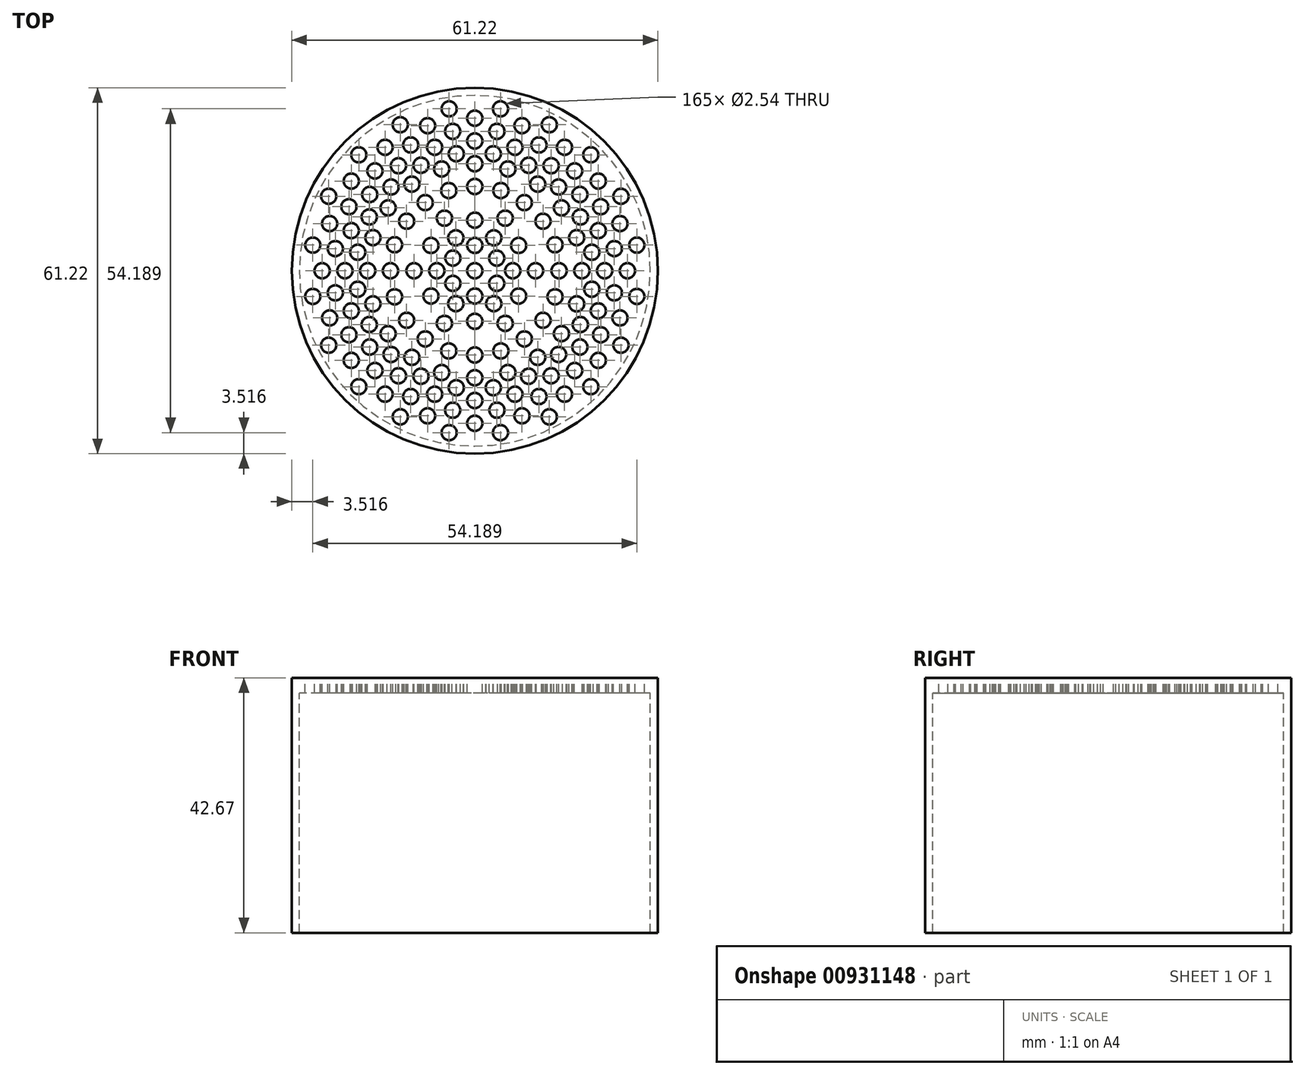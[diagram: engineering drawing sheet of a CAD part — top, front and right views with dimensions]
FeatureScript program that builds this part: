
annotation { "Feature Type Name" : "Feature", "Feature Type Description" : "" }
export const myFeature = defineFeature(function(context is Context, id is Id, definition is map)
    precondition{}
    {
        {
            var Q0;
            Q0=qCreatedBy(makeId("Top.planeOp"),FACE);
            var sketch = newSketch(context, id + "F0", { "sketchPlane" : qUnion([Q0])});
            skCircle(sketch, "E0", {"center": v(0, 0) * mm, "radius": 29.34 * mm});
            skCircle(sketch, "E1", {"center": v(0, 0) * mm, "radius": 30.6 * mm});
            skSolve(sketch);
        }
        {
            var Q0;
            Q0 = qSketchRegion(id + "F0", true);
            extrude(context, id + "F1", {"entities" : qUnion([Q0]), "oppositeDirection" : true, "depth" : 42.67 * mm, "offsetDistance" : 25.4 * mm});
        }
        {
            var Q0;
            Q0=qCreatedBy(makeId("Top.planeOp"),FACE);
            var sketch = newSketch(context, id + "F2", { "sketchPlane" : qUnion([Q0])});
            skCircle(sketch, "E2", {"center": v(0, 0) * mm, "radius": 29.34 * mm});
            skCircle(sketch, "E3", {"center": v(0, 0) * mm, "radius": 1.27 * mm});
            skCircle(sketch, "E4", {"center": v(0, -14.1) * mm, "radius": 1.27 * mm});
            skCircle(sketch, "E5", {"center": v(0, -17.9) * mm, "radius": 1.27 * mm});
            skCircle(sketch, "E6", {"center": v(0, -21.72) * mm, "radius": 1.27 * mm});
            skCircle(sketch, "E7", {"center": v(0, -25.53) * mm, "radius": 1.27 * mm});
            skPoint(sketch, "E8", {"position": v(0, -29.34) * mm});
            skPoint(sketch, "E9.center", {"position": v(0, -2.92) * mm});
            skLineSegment(sketch, "E9.anchor1", {"start": v(0, -2.92) * mm, "end": v(0, -21.72) * mm, "construction": true});
            skCircle(sketch, "E10.1.2", {"center": v(7.89, -24.28) * mm, "radius": 1.27 * mm});
            skCircle(sketch, "E10.1.3", {"center": v(6.71, -20.65) * mm, "radius": 1.27 * mm});
            skCircle(sketch, "E10.1.4", {"center": v(4.36, -13.4) * mm, "radius": 1.27 * mm});
            skCircle(sketch, "E10.1.5", {"center": v(5.53, -17.03) * mm, "radius": 1.27 * mm});
            skPoint(sketch, "E10.1.6", {"position": v(0.9, -2.78) * mm});
            skLineSegment(sketch, "E10.1.7", {"start": v(0.9, -2.78) * mm, "end": v(6.71, -20.65) * mm, "construction": true});
            skCircle(sketch, "E10.2.2", {"center": v(15, -20.65) * mm, "radius": 1.27 * mm});
            skCircle(sketch, "E10.2.3", {"center": v(12.76, -17.57) * mm, "radius": 1.27 * mm});
            skCircle(sketch, "E10.2.4", {"center": v(8.29, -11.4) * mm, "radius": 1.27 * mm});
            skCircle(sketch, "E10.2.5", {"center": v(10.53, -14.49) * mm, "radius": 1.27 * mm});
            skPoint(sketch, "E10.2.6", {"position": v(1.72, -2.36) * mm});
            skLineSegment(sketch, "E10.2.7", {"start": v(1.72, -2.36) * mm, "end": v(12.76, -17.57) * mm, "construction": true});
            skCircle(sketch, "E11.4.3.0", {"center": v(20.65, -15) * mm, "radius": 1.27 * mm});
            skCircle(sketch, "E11.6.3.0", {"center": v(17.57, -12.76) * mm, "radius": 1.27 * mm});
            skCircle(sketch, "E11.8.3.0", {"center": v(11.4, -8.29) * mm, "radius": 1.27 * mm});
            skCircle(sketch, "E11.10.3.0", {"center": v(14.49, -10.53) * mm, "radius": 1.27 * mm});
            skPoint(sketch, "E11.12.3.0", {"position": v(2.36, -1.72) * mm});
            skLineSegment(sketch, "E11.13.3.0", {"start": v(2.36, -1.72) * mm, "end": v(17.57, -12.76) * mm, "construction": true});
            skCircle(sketch, "E11.4.4.0", {"center": v(24.28, -7.89) * mm, "radius": 1.27 * mm});
            skCircle(sketch, "E11.6.4.0", {"center": v(20.65, -6.71) * mm, "radius": 1.27 * mm});
            skCircle(sketch, "E11.8.4.0", {"center": v(13.4, -4.36) * mm, "radius": 1.27 * mm});
            skCircle(sketch, "E11.10.4.0", {"center": v(17.03, -5.53) * mm, "radius": 1.27 * mm});
            skPoint(sketch, "E11.12.4.0", {"position": v(2.78, -0.9) * mm});
            skLineSegment(sketch, "E11.13.4.0", {"start": v(2.78, -0.9) * mm, "end": v(20.65, -6.71) * mm, "construction": true});
            skCircle(sketch, "E11.4.5.0", {"center": v(25.53, 0) * mm, "radius": 1.27 * mm});
            skCircle(sketch, "E11.6.5.0", {"center": v(21.72, 0) * mm, "radius": 1.27 * mm});
            skCircle(sketch, "E11.8.5.0", {"center": v(14.1, 0) * mm, "radius": 1.27 * mm});
            skCircle(sketch, "E11.10.5.0", {"center": v(17.9, 0) * mm, "radius": 1.27 * mm});
            skPoint(sketch, "E11.12.5.0", {"position": v(2.92, 0) * mm});
            skLineSegment(sketch, "E11.13.5.0", {"start": v(2.92, 0) * mm, "end": v(21.72, 0) * mm, "construction": true});
            skCircle(sketch, "E11.4.6.0", {"center": v(24.28, 7.89) * mm, "radius": 1.27 * mm});
            skCircle(sketch, "E11.6.6.0", {"center": v(20.65, 6.71) * mm, "radius": 1.27 * mm});
            skCircle(sketch, "E11.8.6.0", {"center": v(13.4, 4.36) * mm, "radius": 1.27 * mm});
            skCircle(sketch, "E11.10.6.0", {"center": v(17.03, 5.53) * mm, "radius": 1.27 * mm});
            skPoint(sketch, "E11.12.6.0", {"position": v(2.78, 0.9) * mm});
            skLineSegment(sketch, "E11.13.6.0", {"start": v(2.78, 0.9) * mm, "end": v(20.65, 6.71) * mm, "construction": true});
            skCircle(sketch, "E11.4.7.0", {"center": v(20.65, 15) * mm, "radius": 1.27 * mm});
            skCircle(sketch, "E11.6.7.0", {"center": v(17.57, 12.76) * mm, "radius": 1.27 * mm});
            skCircle(sketch, "E11.8.7.0", {"center": v(11.4, 8.29) * mm, "radius": 1.27 * mm});
            skCircle(sketch, "E11.10.7.0", {"center": v(14.49, 10.53) * mm, "radius": 1.27 * mm});
            skPoint(sketch, "E11.12.7.0", {"position": v(2.36, 1.72) * mm});
            skLineSegment(sketch, "E11.13.7.0", {"start": v(2.36, 1.72) * mm, "end": v(17.57, 12.76) * mm, "construction": true});
            skCircle(sketch, "E12.4.8.0", {"center": v(15, 20.65) * mm, "radius": 1.27 * mm});
            skCircle(sketch, "E12.6.8.0", {"center": v(12.76, 17.57) * mm, "radius": 1.27 * mm});
            skCircle(sketch, "E12.8.8.0", {"center": v(8.29, 11.4) * mm, "radius": 1.27 * mm});
            skCircle(sketch, "E12.10.8.0", {"center": v(10.53, 14.49) * mm, "radius": 1.27 * mm});
            skPoint(sketch, "E12.12.8.0", {"position": v(1.72, 2.36) * mm});
            skLineSegment(sketch, "E12.13.8.0", {"start": v(1.72, 2.36) * mm, "end": v(12.76, 17.57) * mm, "construction": true});
            skCircle(sketch, "E12.4.9.0", {"center": v(7.89, 24.28) * mm, "radius": 1.27 * mm});
            skCircle(sketch, "E12.6.9.0", {"center": v(6.71, 20.65) * mm, "radius": 1.27 * mm});
            skCircle(sketch, "E12.8.9.0", {"center": v(4.36, 13.4) * mm, "radius": 1.27 * mm});
            skCircle(sketch, "E12.10.9.0", {"center": v(5.53, 17.03) * mm, "radius": 1.27 * mm});
            skPoint(sketch, "E12.12.9.0", {"position": v(0.9, 2.78) * mm});
            skLineSegment(sketch, "E12.13.9.0", {"start": v(0.9, 2.78) * mm, "end": v(6.71, 20.65) * mm, "construction": true});
            skCircle(sketch, "E12.4.10.0", {"center": v(0, 25.53) * mm, "radius": 1.27 * mm});
            skCircle(sketch, "E12.6.10.0", {"center": v(0, 21.72) * mm, "radius": 1.27 * mm});
            skCircle(sketch, "E12.8.10.0", {"center": v(0, 14.1) * mm, "radius": 1.27 * mm});
            skCircle(sketch, "E12.10.10.0", {"center": v(0, 17.9) * mm, "radius": 1.27 * mm});
            skPoint(sketch, "E12.12.10.0", {"position": v(0, 2.92) * mm});
            skLineSegment(sketch, "E12.13.10.0", {"start": v(0, 2.92) * mm, "end": v(0, 21.72) * mm, "construction": true});
            skCircle(sketch, "E12.4.11.0", {"center": v(-7.89, 24.28) * mm, "radius": 1.27 * mm});
            skCircle(sketch, "E12.6.11.0", {"center": v(-6.71, 20.65) * mm, "radius": 1.27 * mm});
            skCircle(sketch, "E12.8.11.0", {"center": v(-4.36, 13.4) * mm, "radius": 1.27 * mm});
            skCircle(sketch, "E12.10.11.0", {"center": v(-5.53, 17.03) * mm, "radius": 1.27 * mm});
            skPoint(sketch, "E12.12.11.0", {"position": v(-0.9, 2.78) * mm});
            skLineSegment(sketch, "E12.13.11.0", {"start": v(-0.9, 2.78) * mm, "end": v(-6.71, 20.65) * mm, "construction": true});
            skCircle(sketch, "E12.4.12.0", {"center": v(-15, 20.65) * mm, "radius": 1.27 * mm});
            skCircle(sketch, "E12.6.12.0", {"center": v(-12.76, 17.57) * mm, "radius": 1.27 * mm});
            skCircle(sketch, "E12.8.12.0", {"center": v(-8.29, 11.4) * mm, "radius": 1.27 * mm});
            skCircle(sketch, "E12.10.12.0", {"center": v(-10.53, 14.49) * mm, "radius": 1.27 * mm});
            skPoint(sketch, "E12.12.12.0", {"position": v(-1.72, 2.36) * mm});
            skLineSegment(sketch, "E12.13.12.0", {"start": v(-1.72, 2.36) * mm, "end": v(-12.76, 17.57) * mm, "construction": true});
            skCircle(sketch, "E12.4.13.0", {"center": v(-20.65, 15) * mm, "radius": 1.27 * mm});
            skCircle(sketch, "E12.6.13.0", {"center": v(-17.57, 12.76) * mm, "radius": 1.27 * mm});
            skCircle(sketch, "E12.8.13.0", {"center": v(-11.4, 8.29) * mm, "radius": 1.27 * mm});
            skCircle(sketch, "E12.10.13.0", {"center": v(-14.49, 10.53) * mm, "radius": 1.27 * mm});
            skPoint(sketch, "E12.12.13.0", {"position": v(-2.36, 1.72) * mm});
            skLineSegment(sketch, "E12.13.13.0", {"start": v(-2.36, 1.72) * mm, "end": v(-17.57, 12.76) * mm, "construction": true});
            skCircle(sketch, "E12.4.14.0", {"center": v(-24.28, 7.89) * mm, "radius": 1.27 * mm});
            skCircle(sketch, "E12.6.14.0", {"center": v(-20.65, 6.71) * mm, "radius": 1.27 * mm});
            skCircle(sketch, "E12.8.14.0", {"center": v(-13.4, 4.36) * mm, "radius": 1.27 * mm});
            skCircle(sketch, "E12.10.14.0", {"center": v(-17.03, 5.53) * mm, "radius": 1.27 * mm});
            skPoint(sketch, "E12.12.14.0", {"position": v(-2.78, 0.9) * mm});
            skLineSegment(sketch, "E12.13.14.0", {"start": v(-2.78, 0.9) * mm, "end": v(-20.65, 6.71) * mm, "construction": true});
            skCircle(sketch, "E12.4.15.0", {"center": v(-25.53, 0) * mm, "radius": 1.27 * mm});
            skCircle(sketch, "E12.6.15.0", {"center": v(-21.72, 0) * mm, "radius": 1.27 * mm});
            skCircle(sketch, "E12.8.15.0", {"center": v(-14.1, 0) * mm, "radius": 1.27 * mm});
            skCircle(sketch, "E12.10.15.0", {"center": v(-17.9, 0) * mm, "radius": 1.27 * mm});
            skPoint(sketch, "E12.12.15.0", {"position": v(-2.92, 0) * mm});
            skLineSegment(sketch, "E12.13.15.0", {"start": v(-2.92, 0) * mm, "end": v(-21.72, 0) * mm, "construction": true});
            skCircle(sketch, "E13.4.16.0", {"center": v(-24.28, -7.89) * mm, "radius": 1.27 * mm});
            skCircle(sketch, "E13.6.16.0", {"center": v(-20.65, -6.71) * mm, "radius": 1.27 * mm});
            skCircle(sketch, "E13.8.16.0", {"center": v(-13.4, -4.36) * mm, "radius": 1.27 * mm});
            skCircle(sketch, "E13.10.16.0", {"center": v(-17.03, -5.53) * mm, "radius": 1.27 * mm});
            skPoint(sketch, "E13.12.16.0", {"position": v(-2.78, -0.9) * mm});
            skLineSegment(sketch, "E13.13.16.0", {"start": v(-2.78, -0.9) * mm, "end": v(-20.65, -6.71) * mm, "construction": true});
            skCircle(sketch, "E13.4.17.0", {"center": v(-20.65, -15) * mm, "radius": 1.27 * mm});
            skCircle(sketch, "E13.6.17.0", {"center": v(-17.57, -12.76) * mm, "radius": 1.27 * mm});
            skCircle(sketch, "E13.8.17.0", {"center": v(-11.4, -8.29) * mm, "radius": 1.27 * mm});
            skCircle(sketch, "E13.10.17.0", {"center": v(-14.49, -10.53) * mm, "radius": 1.27 * mm});
            skPoint(sketch, "E13.12.17.0", {"position": v(-2.36, -1.72) * mm});
            skLineSegment(sketch, "E13.13.17.0", {"start": v(-2.36, -1.72) * mm, "end": v(-17.57, -12.76) * mm, "construction": true});
            skCircle(sketch, "E13.4.18.0", {"center": v(-15, -20.65) * mm, "radius": 1.27 * mm});
            skCircle(sketch, "E13.6.18.0", {"center": v(-12.76, -17.57) * mm, "radius": 1.27 * mm});
            skCircle(sketch, "E13.8.18.0", {"center": v(-8.29, -11.4) * mm, "radius": 1.27 * mm});
            skCircle(sketch, "E13.10.18.0", {"center": v(-10.53, -14.49) * mm, "radius": 1.27 * mm});
            skPoint(sketch, "E13.12.18.0", {"position": v(-1.72, -2.36) * mm});
            skLineSegment(sketch, "E13.13.18.0", {"start": v(-1.72, -2.36) * mm, "end": v(-12.76, -17.57) * mm, "construction": true});
            skCircle(sketch, "E13.4.19.0", {"center": v(-7.89, -24.28) * mm, "radius": 1.27 * mm});
            skCircle(sketch, "E13.6.19.0", {"center": v(-6.71, -20.65) * mm, "radius": 1.27 * mm});
            skCircle(sketch, "E13.8.19.0", {"center": v(-4.36, -13.4) * mm, "radius": 1.27 * mm});
            skCircle(sketch, "E13.10.19.0", {"center": v(-5.53, -17.03) * mm, "radius": 1.27 * mm});
            skPoint(sketch, "E13.12.19.0", {"position": v(-0.9, -2.78) * mm});
            skLineSegment(sketch, "E13.13.19.0", {"start": v(-0.9, -2.78) * mm, "end": v(-6.71, -20.65) * mm, "construction": true});
            skSolve(sketch);
        }
        {
            var Q0;
            Q0 = qSketchRegion(id + "F2", true);
            extrude(context, id + "F3", {"entities" : qUnion([Q0]), "operationType" : NewBodyOperationType.ADD, "oppositeDirection" : true, "depth" : 2.54 * mm, "offsetDistance" : 25.4 * mm});
        }
        {
            var Q0;
            Q0=makeQuery(id+"F3.opExtrude","CAP_FACE",FACE,{"disambiguationData":[OSD([sQuery(id+"F2.wireOp",EDGE,"E2"),sQuery(id+"F2.wireOp",EDGE,"E4"),sQuery(id+"F2.wireOp",EDGE,"E5"),sQuery(id+"F2.wireOp",EDGE,"E6"),sQuery(id+"F2.wireOp",EDGE,"E7"),sQuery(id+"F2.wireOp",EDGE,"E10.1.2"),sQuery(id+"F2.wireOp",EDGE,"E10.1.3"),sQuery(id+"F2.wireOp",EDGE,"E10.1.4"),sQuery(id+"F2.wireOp",EDGE,"E10.1.5"),sQuery(id+"F2.wireOp",EDGE,"E10.2.2"),sQuery(id+"F2.wireOp",EDGE,"E10.2.3"),sQuery(id+"F2.wireOp",EDGE,"E10.2.4"),sQuery(id+"F2.wireOp",EDGE,"E10.2.5"),sQuery(id+"F2.wireOp",EDGE,"E11.4.3.0"),sQuery(id+"F2.wireOp",EDGE,"E11.6.3.0"),sQuery(id+"F2.wireOp",EDGE,"E11.8.3.0"),sQuery(id+"F2.wireOp",EDGE,"E11.10.3.0"),sQuery(id+"F2.wireOp",EDGE,"E11.4.4.0"),sQuery(id+"F2.wireOp",EDGE,"E11.6.4.0"),sQuery(id+"F2.wireOp",EDGE,"E11.8.4.0"),sQuery(id+"F2.wireOp",EDGE,"E11.10.4.0"),sQuery(id+"F2.wireOp",EDGE,"E11.4.5.0"),sQuery(id+"F2.wireOp",EDGE,"E11.6.5.0"),sQuery(id+"F2.wireOp",EDGE,"E11.8.5.0"),sQuery(id+"F2.wireOp",EDGE,"E11.10.5.0"),sQuery(id+"F2.wireOp",EDGE,"E11.4.6.0"),sQuery(id+"F2.wireOp",EDGE,"E11.6.6.0"),sQuery(id+"F2.wireOp",EDGE,"E11.8.6.0"),sQuery(id+"F2.wireOp",EDGE,"E11.10.6.0"),sQuery(id+"F2.wireOp",EDGE,"E11.4.7.0"),sQuery(id+"F2.wireOp",EDGE,"E11.6.7.0"),sQuery(id+"F2.wireOp",EDGE,"E11.8.7.0"),sQuery(id+"F2.wireOp",EDGE,"E11.10.7.0"),sQuery(id+"F2.wireOp",EDGE,"E12.4.8.0"),sQuery(id+"F2.wireOp",EDGE,"E12.6.8.0"),sQuery(id+"F2.wireOp",EDGE,"E12.8.8.0"),sQuery(id+"F2.wireOp",EDGE,"E12.10.8.0"),sQuery(id+"F2.wireOp",EDGE,"E12.4.9.0"),sQuery(id+"F2.wireOp",EDGE,"E12.6.9.0"),sQuery(id+"F2.wireOp",EDGE,"E12.8.9.0"),sQuery(id+"F2.wireOp",EDGE,"E12.10.9.0"),sQuery(id+"F2.wireOp",EDGE,"E12.4.10.0"),sQuery(id+"F2.wireOp",EDGE,"E12.6.10.0"),sQuery(id+"F2.wireOp",EDGE,"E12.8.10.0"),sQuery(id+"F2.wireOp",EDGE,"E12.10.10.0"),sQuery(id+"F2.wireOp",EDGE,"E12.4.11.0"),sQuery(id+"F2.wireOp",EDGE,"E12.6.11.0"),sQuery(id+"F2.wireOp",EDGE,"E12.8.11.0"),sQuery(id+"F2.wireOp",EDGE,"E12.10.11.0"),sQuery(id+"F2.wireOp",EDGE,"E12.4.12.0"),sQuery(id+"F2.wireOp",EDGE,"E12.6.12.0"),sQuery(id+"F2.wireOp",EDGE,"E12.8.12.0"),sQuery(id+"F2.wireOp",EDGE,"E12.10.12.0"),sQuery(id+"F2.wireOp",EDGE,"E12.4.13.0"),sQuery(id+"F2.wireOp",EDGE,"E12.6.13.0"),sQuery(id+"F2.wireOp",EDGE,"E12.8.13.0"),sQuery(id+"F2.wireOp",EDGE,"E12.10.13.0"),sQuery(id+"F2.wireOp",EDGE,"E12.4.14.0"),sQuery(id+"F2.wireOp",EDGE,"E12.6.14.0"),sQuery(id+"F2.wireOp",EDGE,"E12.8.14.0"),sQuery(id+"F2.wireOp",EDGE,"E12.10.14.0"),sQuery(id+"F2.wireOp",EDGE,"E12.4.15.0"),sQuery(id+"F2.wireOp",EDGE,"E12.6.15.0"),sQuery(id+"F2.wireOp",EDGE,"E12.8.15.0"),sQuery(id+"F2.wireOp",EDGE,"E12.10.15.0"),sQuery(id+"F2.wireOp",EDGE,"E13.4.16.0"),sQuery(id+"F2.wireOp",EDGE,"E13.6.16.0"),sQuery(id+"F2.wireOp",EDGE,"E13.8.16.0"),sQuery(id+"F2.wireOp",EDGE,"E13.10.16.0"),sQuery(id+"F2.wireOp",EDGE,"E13.4.17.0"),sQuery(id+"F2.wireOp",EDGE,"E13.6.17.0"),sQuery(id+"F2.wireOp",EDGE,"E13.8.17.0"),sQuery(id+"F2.wireOp",EDGE,"E13.10.17.0"),sQuery(id+"F2.wireOp",EDGE,"E13.4.18.0"),sQuery(id+"F2.wireOp",EDGE,"E13.6.18.0"),sQuery(id+"F2.wireOp",EDGE,"E13.8.18.0"),sQuery(id+"F2.wireOp",EDGE,"E13.10.18.0"),sQuery(id+"F2.wireOp",EDGE,"E13.4.19.0"),sQuery(id+"F2.wireOp",EDGE,"E3"),sQuery(id+"F2.wireOp",EDGE,"E13.6.19.0"),sQuery(id+"F2.wireOp",EDGE,"E13.8.19.0"),sQuery(id+"F2.wireOp",EDGE,"E13.10.19.0")])],"isStart":true});
            var sketch = newSketch(context, id + "F4", { "sketchPlane" : qUnion([Q0])});
            skCircle(sketch, "E14", {"center": v(-3.7, -23.33) * mm, "radius": 1.27 * mm});
            skCircle(sketch, "E15", {"center": v(-4.3, -27.1) * mm, "radius": 1.27 * mm});
            skLineSegment(sketch, "E16", {"start": v(0, 0) * mm, "end": v(-5.46, -34.46) * mm});
            skPoint(sketch, "E17", {"position": v(-4.59, -28.98) * mm});
            skCircle(sketch, "E18.1.0", {"center": v(4.3, -27.1) * mm, "radius": 1.27 * mm});
            skCircle(sketch, "E18.1.1", {"center": v(3.7, -23.33) * mm, "radius": 1.27 * mm});
            skCircle(sketch, "E18.2.0", {"center": v(12.45, -24.44) * mm, "radius": 1.27 * mm});
            skCircle(sketch, "E18.2.1", {"center": v(10.72, -21.05) * mm, "radius": 1.27 * mm});
            skCircle(sketch, "E18.3.0", {"center": v(19.4, -19.4) * mm, "radius": 1.27 * mm});
            skCircle(sketch, "E18.3.1", {"center": v(16.7, -16.7) * mm, "radius": 1.27 * mm});
            skCircle(sketch, "E18.4.0", {"center": v(24.44, -12.45) * mm, "radius": 1.27 * mm});
            skCircle(sketch, "E18.4.1", {"center": v(21.05, -10.72) * mm, "radius": 1.27 * mm});
            skCircle(sketch, "E18.5.0", {"center": v(27.1, -4.3) * mm, "radius": 1.27 * mm});
            skCircle(sketch, "E18.5.1", {"center": v(23.33, -3.7) * mm, "radius": 1.27 * mm});
            skCircle(sketch, "E18.6.0", {"center": v(27.1, 4.3) * mm, "radius": 1.27 * mm});
            skCircle(sketch, "E18.6.1", {"center": v(23.33, 3.7) * mm, "radius": 1.27 * mm});
            skCircle(sketch, "E18.7.0", {"center": v(24.44, 12.45) * mm, "radius": 1.27 * mm});
            skCircle(sketch, "E18.7.1", {"center": v(21.05, 10.72) * mm, "radius": 1.27 * mm});
            skCircle(sketch, "E18.8.0", {"center": v(19.4, 19.4) * mm, "radius": 1.27 * mm});
            skCircle(sketch, "E18.8.1", {"center": v(16.7, 16.7) * mm, "radius": 1.27 * mm});
            skCircle(sketch, "E18.9.0", {"center": v(12.45, 24.44) * mm, "radius": 1.27 * mm});
            skCircle(sketch, "E18.9.1", {"center": v(10.72, 21.05) * mm, "radius": 1.27 * mm});
            skCircle(sketch, "E18.10.0", {"center": v(4.3, 27.1) * mm, "radius": 1.27 * mm});
            skCircle(sketch, "E18.10.1", {"center": v(3.7, 23.33) * mm, "radius": 1.27 * mm});
            skCircle(sketch, "E18.11.0", {"center": v(-4.3, 27.1) * mm, "radius": 1.27 * mm});
            skCircle(sketch, "E18.11.1", {"center": v(-3.7, 23.33) * mm, "radius": 1.27 * mm});
            skCircle(sketch, "E18.12.0", {"center": v(-12.45, 24.44) * mm, "radius": 1.27 * mm});
            skCircle(sketch, "E18.12.1", {"center": v(-10.72, 21.05) * mm, "radius": 1.27 * mm});
            skCircle(sketch, "E18.13.0", {"center": v(-19.4, 19.4) * mm, "radius": 1.27 * mm});
            skCircle(sketch, "E18.13.1", {"center": v(-16.7, 16.7) * mm, "radius": 1.27 * mm});
            skCircle(sketch, "E18.14.0", {"center": v(-24.44, 12.45) * mm, "radius": 1.27 * mm});
            skCircle(sketch, "E18.14.1", {"center": v(-21.05, 10.72) * mm, "radius": 1.27 * mm});
            skCircle(sketch, "E18.15.0", {"center": v(-27.1, 4.3) * mm, "radius": 1.27 * mm});
            skCircle(sketch, "E18.15.1", {"center": v(-23.33, 3.7) * mm, "radius": 1.27 * mm});
            skCircle(sketch, "E18.16.0", {"center": v(-27.1, -4.3) * mm, "radius": 1.27 * mm});
            skCircle(sketch, "E18.16.1", {"center": v(-23.33, -3.7) * mm, "radius": 1.27 * mm});
            skCircle(sketch, "E18.17.0", {"center": v(-24.44, -12.45) * mm, "radius": 1.27 * mm});
            skCircle(sketch, "E18.17.1", {"center": v(-21.05, -10.72) * mm, "radius": 1.27 * mm});
            skCircle(sketch, "E18.18.0", {"center": v(-19.4, -19.4) * mm, "radius": 1.27 * mm});
            skCircle(sketch, "E18.18.1", {"center": v(-16.7, -16.7) * mm, "radius": 1.27 * mm});
            skCircle(sketch, "E18.19.0", {"center": v(-12.45, -24.44) * mm, "radius": 1.27 * mm});
            skCircle(sketch, "E18.19.1", {"center": v(-10.72, -21.05) * mm, "radius": 1.27 * mm});
            skPoint(sketch, "E18.center", {"position": v(0, 0) * mm});
            skCircle(sketch, "E19", {"center": v(-3.1, -19.57) * mm, "radius": 1.27 * mm});
            skCircle(sketch, "E20.1.0", {"center": v(3.1, -19.57) * mm, "radius": 1.27 * mm});
            skCircle(sketch, "E20.2.0", {"center": v(9, -17.65) * mm, "radius": 1.27 * mm});
            skCircle(sketch, "E20.3.0", {"center": v(14, -14) * mm, "radius": 1.27 * mm});
            skCircle(sketch, "E20.4.0", {"center": v(17.65, -9) * mm, "radius": 1.27 * mm});
            skCircle(sketch, "E20.5.0", {"center": v(19.57, -3.1) * mm, "radius": 1.27 * mm});
            skCircle(sketch, "E20.6.0", {"center": v(19.57, 3.1) * mm, "radius": 1.27 * mm});
            skCircle(sketch, "E20.7.0", {"center": v(17.65, 9) * mm, "radius": 1.27 * mm});
            skCircle(sketch, "E20.8.0", {"center": v(14, 14) * mm, "radius": 1.27 * mm});
            skCircle(sketch, "E20.9.0", {"center": v(9, 17.65) * mm, "radius": 1.27 * mm});
            skCircle(sketch, "E20.10.0", {"center": v(3.1, 19.57) * mm, "radius": 1.27 * mm});
            skCircle(sketch, "E20.11.0", {"center": v(-3.1, 19.57) * mm, "radius": 1.27 * mm});
            skCircle(sketch, "E20.12.0", {"center": v(-9, 17.65) * mm, "radius": 1.27 * mm});
            skCircle(sketch, "E20.13.0", {"center": v(-14, 14) * mm, "radius": 1.27 * mm});
            skCircle(sketch, "E20.14.0", {"center": v(-17.65, 9) * mm, "radius": 1.27 * mm});
            skCircle(sketch, "E20.15.0", {"center": v(-19.57, 3.1) * mm, "radius": 1.27 * mm});
            skCircle(sketch, "E20.16.0", {"center": v(-19.57, -3.1) * mm, "radius": 1.27 * mm});
            skCircle(sketch, "E20.17.0", {"center": v(-17.65, -9) * mm, "radius": 1.27 * mm});
            skCircle(sketch, "E20.18.0", {"center": v(-14, -14) * mm, "radius": 1.27 * mm});
            skCircle(sketch, "E20.19.0", {"center": v(-9, -17.65) * mm, "radius": 1.27 * mm});
            skSolve(sketch);
        }
        {
            var Q0;
            Q0=makeQuery(id+"F3.opExtrude","CAP_FACE",FACE,{"disambiguationData":[OSD([sQuery(id+"F2.wireOp",EDGE,"E2"),sQuery(id+"F2.wireOp",EDGE,"E4"),sQuery(id+"F2.wireOp",EDGE,"E5"),sQuery(id+"F2.wireOp",EDGE,"E6"),sQuery(id+"F2.wireOp",EDGE,"E7"),sQuery(id+"F2.wireOp",EDGE,"E10.1.2"),sQuery(id+"F2.wireOp",EDGE,"E10.1.3"),sQuery(id+"F2.wireOp",EDGE,"E10.1.4"),sQuery(id+"F2.wireOp",EDGE,"E10.1.5"),sQuery(id+"F2.wireOp",EDGE,"E10.2.2"),sQuery(id+"F2.wireOp",EDGE,"E10.2.3"),sQuery(id+"F2.wireOp",EDGE,"E10.2.4"),sQuery(id+"F2.wireOp",EDGE,"E10.2.5"),sQuery(id+"F2.wireOp",EDGE,"E11.4.3.0"),sQuery(id+"F2.wireOp",EDGE,"E11.6.3.0"),sQuery(id+"F2.wireOp",EDGE,"E11.8.3.0"),sQuery(id+"F2.wireOp",EDGE,"E11.10.3.0"),sQuery(id+"F2.wireOp",EDGE,"E11.4.4.0"),sQuery(id+"F2.wireOp",EDGE,"E11.6.4.0"),sQuery(id+"F2.wireOp",EDGE,"E11.8.4.0"),sQuery(id+"F2.wireOp",EDGE,"E11.10.4.0"),sQuery(id+"F2.wireOp",EDGE,"E11.4.5.0"),sQuery(id+"F2.wireOp",EDGE,"E11.6.5.0"),sQuery(id+"F2.wireOp",EDGE,"E11.8.5.0"),sQuery(id+"F2.wireOp",EDGE,"E11.10.5.0"),sQuery(id+"F2.wireOp",EDGE,"E11.4.6.0"),sQuery(id+"F2.wireOp",EDGE,"E11.6.6.0"),sQuery(id+"F2.wireOp",EDGE,"E11.8.6.0"),sQuery(id+"F2.wireOp",EDGE,"E11.10.6.0"),sQuery(id+"F2.wireOp",EDGE,"E11.4.7.0"),sQuery(id+"F2.wireOp",EDGE,"E11.6.7.0"),sQuery(id+"F2.wireOp",EDGE,"E11.8.7.0"),sQuery(id+"F2.wireOp",EDGE,"E11.10.7.0"),sQuery(id+"F2.wireOp",EDGE,"E12.4.8.0"),sQuery(id+"F2.wireOp",EDGE,"E12.6.8.0"),sQuery(id+"F2.wireOp",EDGE,"E12.8.8.0"),sQuery(id+"F2.wireOp",EDGE,"E12.10.8.0"),sQuery(id+"F2.wireOp",EDGE,"E12.4.9.0"),sQuery(id+"F2.wireOp",EDGE,"E12.6.9.0"),sQuery(id+"F2.wireOp",EDGE,"E12.8.9.0"),sQuery(id+"F2.wireOp",EDGE,"E12.10.9.0"),sQuery(id+"F2.wireOp",EDGE,"E12.4.10.0"),sQuery(id+"F2.wireOp",EDGE,"E12.6.10.0"),sQuery(id+"F2.wireOp",EDGE,"E12.8.10.0"),sQuery(id+"F2.wireOp",EDGE,"E12.10.10.0"),sQuery(id+"F2.wireOp",EDGE,"E12.4.11.0"),sQuery(id+"F2.wireOp",EDGE,"E12.6.11.0"),sQuery(id+"F2.wireOp",EDGE,"E12.8.11.0"),sQuery(id+"F2.wireOp",EDGE,"E12.10.11.0"),sQuery(id+"F2.wireOp",EDGE,"E12.4.12.0"),sQuery(id+"F2.wireOp",EDGE,"E12.6.12.0"),sQuery(id+"F2.wireOp",EDGE,"E12.8.12.0"),sQuery(id+"F2.wireOp",EDGE,"E12.10.12.0"),sQuery(id+"F2.wireOp",EDGE,"E12.4.13.0"),sQuery(id+"F2.wireOp",EDGE,"E12.6.13.0"),sQuery(id+"F2.wireOp",EDGE,"E12.8.13.0"),sQuery(id+"F2.wireOp",EDGE,"E12.10.13.0"),sQuery(id+"F2.wireOp",EDGE,"E12.4.14.0"),sQuery(id+"F2.wireOp",EDGE,"E12.6.14.0"),sQuery(id+"F2.wireOp",EDGE,"E12.8.14.0"),sQuery(id+"F2.wireOp",EDGE,"E12.10.14.0"),sQuery(id+"F2.wireOp",EDGE,"E12.4.15.0"),sQuery(id+"F2.wireOp",EDGE,"E12.6.15.0"),sQuery(id+"F2.wireOp",EDGE,"E12.8.15.0"),sQuery(id+"F2.wireOp",EDGE,"E12.10.15.0"),sQuery(id+"F2.wireOp",EDGE,"E13.4.16.0"),sQuery(id+"F2.wireOp",EDGE,"E13.6.16.0"),sQuery(id+"F2.wireOp",EDGE,"E13.8.16.0"),sQuery(id+"F2.wireOp",EDGE,"E13.10.16.0"),sQuery(id+"F2.wireOp",EDGE,"E13.4.17.0"),sQuery(id+"F2.wireOp",EDGE,"E13.6.17.0"),sQuery(id+"F2.wireOp",EDGE,"E13.8.17.0"),sQuery(id+"F2.wireOp",EDGE,"E13.10.17.0"),sQuery(id+"F2.wireOp",EDGE,"E13.4.18.0"),sQuery(id+"F2.wireOp",EDGE,"E13.6.18.0"),sQuery(id+"F2.wireOp",EDGE,"E13.8.18.0"),sQuery(id+"F2.wireOp",EDGE,"E13.10.18.0"),sQuery(id+"F2.wireOp",EDGE,"E13.4.19.0"),sQuery(id+"F2.wireOp",EDGE,"E3"),sQuery(id+"F2.wireOp",EDGE,"E13.6.19.0"),sQuery(id+"F2.wireOp",EDGE,"E13.8.19.0"),sQuery(id+"F2.wireOp",EDGE,"E13.10.19.0")])],"isStart":true});
            var sketch = newSketch(context, id + "F5", { "sketchPlane" : qUnion([Q0])});
            skCircle(sketch, "E21", {"center": v(0, -4.23) * mm, "radius": 1.27 * mm});
            skCircle(sketch, "E22", {"center": v(0, -8.47) * mm, "radius": 1.27 * mm});
            skCircle(sketch, "E23.1.0", {"center": v(3.67, -2.12) * mm, "radius": 1.27 * mm});
            skCircle(sketch, "E23.1.1", {"center": v(7.33, -4.23) * mm, "radius": 1.27 * mm});
            skCircle(sketch, "E23.2.0", {"center": v(3.67, 2.12) * mm, "radius": 1.27 * mm});
            skCircle(sketch, "E23.2.1", {"center": v(7.33, 4.23) * mm, "radius": 1.27 * mm});
            skCircle(sketch, "E23.3.0", {"center": v(0, 4.23) * mm, "radius": 1.27 * mm});
            skCircle(sketch, "E23.3.1", {"center": v(0, 8.47) * mm, "radius": 1.27 * mm});
            skCircle(sketch, "E23.4.0", {"center": v(-3.67, 2.12) * mm, "radius": 1.27 * mm});
            skCircle(sketch, "E23.4.1", {"center": v(-7.33, 4.23) * mm, "radius": 1.27 * mm});
            skCircle(sketch, "E23.5.0", {"center": v(-3.67, -2.12) * mm, "radius": 1.27 * mm});
            skCircle(sketch, "E23.5.1", {"center": v(-7.33, -4.23) * mm, "radius": 1.27 * mm});
            skPoint(sketch, "E23.center", {"position": v(0, 0) * mm});
            skSolve(sketch);
        }
        {
            var Q0;
            Q0=makeQuery(id+"F3.opExtrude","CAP_FACE",FACE,{"disambiguationData":[OSD([sQuery(id+"F2.wireOp",EDGE,"E2"),sQuery(id+"F2.wireOp",EDGE,"E4"),sQuery(id+"F2.wireOp",EDGE,"E5"),sQuery(id+"F2.wireOp",EDGE,"E6"),sQuery(id+"F2.wireOp",EDGE,"E7"),sQuery(id+"F2.wireOp",EDGE,"E10.1.2"),sQuery(id+"F2.wireOp",EDGE,"E10.1.3"),sQuery(id+"F2.wireOp",EDGE,"E10.1.4"),sQuery(id+"F2.wireOp",EDGE,"E10.1.5"),sQuery(id+"F2.wireOp",EDGE,"E10.2.2"),sQuery(id+"F2.wireOp",EDGE,"E10.2.3"),sQuery(id+"F2.wireOp",EDGE,"E10.2.4"),sQuery(id+"F2.wireOp",EDGE,"E10.2.5"),sQuery(id+"F2.wireOp",EDGE,"E11.4.3.0"),sQuery(id+"F2.wireOp",EDGE,"E11.6.3.0"),sQuery(id+"F2.wireOp",EDGE,"E11.8.3.0"),sQuery(id+"F2.wireOp",EDGE,"E11.10.3.0"),sQuery(id+"F2.wireOp",EDGE,"E11.4.4.0"),sQuery(id+"F2.wireOp",EDGE,"E11.6.4.0"),sQuery(id+"F2.wireOp",EDGE,"E11.8.4.0"),sQuery(id+"F2.wireOp",EDGE,"E11.10.4.0"),sQuery(id+"F2.wireOp",EDGE,"E11.4.5.0"),sQuery(id+"F2.wireOp",EDGE,"E11.6.5.0"),sQuery(id+"F2.wireOp",EDGE,"E11.8.5.0"),sQuery(id+"F2.wireOp",EDGE,"E11.10.5.0"),sQuery(id+"F2.wireOp",EDGE,"E11.4.6.0"),sQuery(id+"F2.wireOp",EDGE,"E11.6.6.0"),sQuery(id+"F2.wireOp",EDGE,"E11.8.6.0"),sQuery(id+"F2.wireOp",EDGE,"E11.10.6.0"),sQuery(id+"F2.wireOp",EDGE,"E11.4.7.0"),sQuery(id+"F2.wireOp",EDGE,"E11.6.7.0"),sQuery(id+"F2.wireOp",EDGE,"E11.8.7.0"),sQuery(id+"F2.wireOp",EDGE,"E11.10.7.0"),sQuery(id+"F2.wireOp",EDGE,"E12.4.8.0"),sQuery(id+"F2.wireOp",EDGE,"E12.6.8.0"),sQuery(id+"F2.wireOp",EDGE,"E12.8.8.0"),sQuery(id+"F2.wireOp",EDGE,"E12.10.8.0"),sQuery(id+"F2.wireOp",EDGE,"E12.4.9.0"),sQuery(id+"F2.wireOp",EDGE,"E12.6.9.0"),sQuery(id+"F2.wireOp",EDGE,"E12.8.9.0"),sQuery(id+"F2.wireOp",EDGE,"E12.10.9.0"),sQuery(id+"F2.wireOp",EDGE,"E12.4.10.0"),sQuery(id+"F2.wireOp",EDGE,"E12.6.10.0"),sQuery(id+"F2.wireOp",EDGE,"E12.8.10.0"),sQuery(id+"F2.wireOp",EDGE,"E12.10.10.0"),sQuery(id+"F2.wireOp",EDGE,"E12.4.11.0"),sQuery(id+"F2.wireOp",EDGE,"E12.6.11.0"),sQuery(id+"F2.wireOp",EDGE,"E12.8.11.0"),sQuery(id+"F2.wireOp",EDGE,"E12.10.11.0"),sQuery(id+"F2.wireOp",EDGE,"E12.4.12.0"),sQuery(id+"F2.wireOp",EDGE,"E12.6.12.0"),sQuery(id+"F2.wireOp",EDGE,"E12.8.12.0"),sQuery(id+"F2.wireOp",EDGE,"E12.10.12.0"),sQuery(id+"F2.wireOp",EDGE,"E12.4.13.0"),sQuery(id+"F2.wireOp",EDGE,"E12.6.13.0"),sQuery(id+"F2.wireOp",EDGE,"E12.8.13.0"),sQuery(id+"F2.wireOp",EDGE,"E12.10.13.0"),sQuery(id+"F2.wireOp",EDGE,"E12.4.14.0"),sQuery(id+"F2.wireOp",EDGE,"E12.6.14.0"),sQuery(id+"F2.wireOp",EDGE,"E12.8.14.0"),sQuery(id+"F2.wireOp",EDGE,"E12.10.14.0"),sQuery(id+"F2.wireOp",EDGE,"E12.4.15.0"),sQuery(id+"F2.wireOp",EDGE,"E12.6.15.0"),sQuery(id+"F2.wireOp",EDGE,"E12.8.15.0"),sQuery(id+"F2.wireOp",EDGE,"E12.10.15.0"),sQuery(id+"F2.wireOp",EDGE,"E13.4.16.0"),sQuery(id+"F2.wireOp",EDGE,"E13.6.16.0"),sQuery(id+"F2.wireOp",EDGE,"E13.8.16.0"),sQuery(id+"F2.wireOp",EDGE,"E13.10.16.0"),sQuery(id+"F2.wireOp",EDGE,"E13.4.17.0"),sQuery(id+"F2.wireOp",EDGE,"E13.6.17.0"),sQuery(id+"F2.wireOp",EDGE,"E13.8.17.0"),sQuery(id+"F2.wireOp",EDGE,"E13.10.17.0"),sQuery(id+"F2.wireOp",EDGE,"E13.4.18.0"),sQuery(id+"F2.wireOp",EDGE,"E13.6.18.0"),sQuery(id+"F2.wireOp",EDGE,"E13.8.18.0"),sQuery(id+"F2.wireOp",EDGE,"E13.10.18.0"),sQuery(id+"F2.wireOp",EDGE,"E13.4.19.0"),sQuery(id+"F2.wireOp",EDGE,"E3"),sQuery(id+"F2.wireOp",EDGE,"E13.6.19.0"),sQuery(id+"F2.wireOp",EDGE,"E13.8.19.0"),sQuery(id+"F2.wireOp",EDGE,"E13.10.19.0")])],"isStart":true});
            var sketch = newSketch(context, id + "F6", { "sketchPlane" : qUnion([Q0])});
            skCircle(sketch, "E24", {"center": v(-6.35, 0) * mm, "radius": 1.27 * mm});
            skCircle(sketch, "E25.1.0", {"center": v(-3.18, -5.5) * mm, "radius": 1.27 * mm});
            skCircle(sketch, "E25.2.0", {"center": v(3.17, -5.5) * mm, "radius": 1.27 * mm});
            skCircle(sketch, "E25.3.0", {"center": v(6.35, 0) * mm, "radius": 1.27 * mm});
            skCircle(sketch, "E25.4.0", {"center": v(3.18, 5.5) * mm, "radius": 1.27 * mm});
            skCircle(sketch, "E25.5.0", {"center": v(-3.18, 5.5) * mm, "radius": 1.27 * mm});
            skPoint(sketch, "E25.center", {"position": v(0, 0) * mm});
            skCircle(sketch, "E26", {"center": v(-10.16, 0) * mm, "radius": 1.27 * mm});
            skCircle(sketch, "E27.1.0", {"center": v(-5.08, -8.8) * mm, "radius": 1.27 * mm});
            skCircle(sketch, "E27.2.0", {"center": v(5.08, -8.8) * mm, "radius": 1.27 * mm});
            skCircle(sketch, "E27.3.0", {"center": v(10.16, 0) * mm, "radius": 1.27 * mm});
            skCircle(sketch, "E27.4.0", {"center": v(5.08, 8.8) * mm, "radius": 1.27 * mm});
            skCircle(sketch, "E27.5.0", {"center": v(-5.08, 8.8) * mm, "radius": 1.27 * mm});
            skSolve(sketch);
        }
        {
            var Q0;
            Q0 = qSketchRegion(id + "F4", true);
            extrude(context, id + "F7", {"entities" : qUnion([Q0]), "operationType" : NewBodyOperationType.REMOVE, "endBound" : BoundingType.UP_TO_NEXT, "oppositeDirection" : true, "depth" : 25.4 * mm, "offsetDistance" : 25.4 * mm});
        }
        {
            var Q0;
            Q0 = qSketchRegion(id + "F5", true);
            extrude(context, id + "F8", {"entities" : qUnion([Q0]), "operationType" : NewBodyOperationType.REMOVE, "endBound" : BoundingType.UP_TO_NEXT, "oppositeDirection" : true, "depth" : 25.4 * mm, "offsetDistance" : 25.4 * mm});
        }
        {
            var Q0;
            Q0 = qSketchRegion(id + "F6", true);
            extrude(context, id + "F9", {"entities" : qUnion([Q0]), "operationType" : NewBodyOperationType.REMOVE, "endBound" : BoundingType.UP_TO_NEXT, "oppositeDirection" : true, "depth" : 25.4 * mm, "offsetDistance" : 25.4 * mm});
        }
    });
